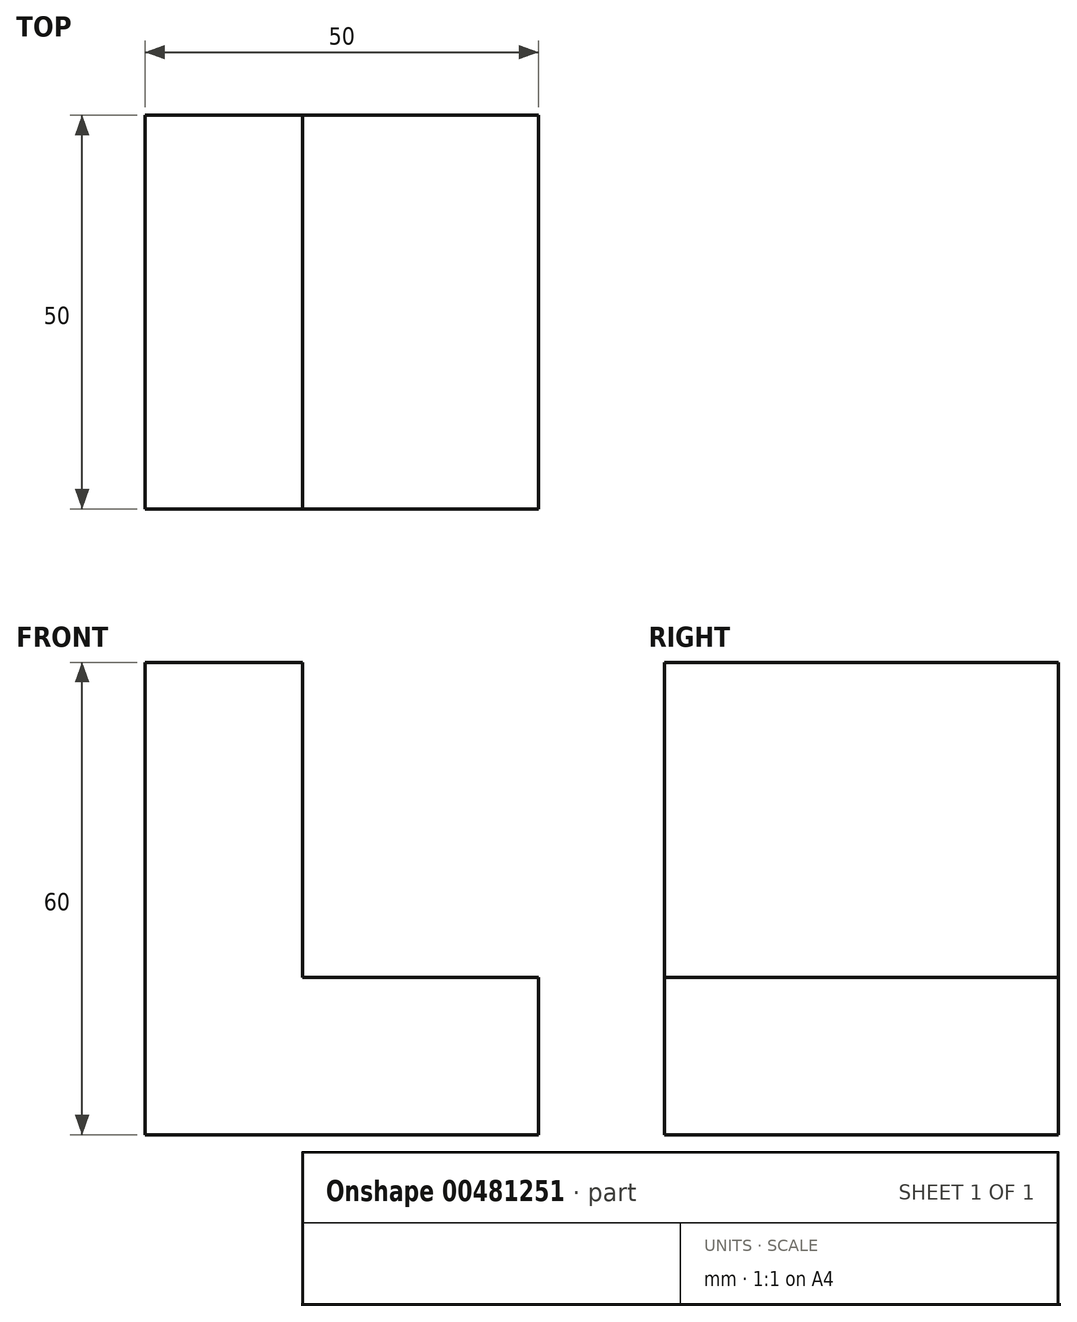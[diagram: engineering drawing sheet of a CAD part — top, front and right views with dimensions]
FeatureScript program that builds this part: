
annotation { "Feature Type Name" : "Feature", "Feature Type Description" : "" }
export const myFeature = defineFeature(function(context is Context, id is Id, definition is map)
    precondition{}
    {
        {
            var Q0;
            Q0=qCreatedBy(makeId("Front.planeOp"),FACE);
            var sketch = newSketch(context, id + "F0", { "sketchPlane" : qUnion([Q0])});
            skLineSegment(sketch, "E0", {"start": v(0, 0) * mm, "end": v(50, 0) * mm});
            skLineSegment(sketch, "E1", {"start": v(50, 0) * mm, "end": v(50, 20) * mm});
            skLineSegment(sketch, "E2", {"start": v(50, 20) * mm, "end": v(20, 20) * mm});
            skLineSegment(sketch, "E3", {"start": v(20, 20) * mm, "end": v(20, 60) * mm});
            skLineSegment(sketch, "E4", {"start": v(20, 60) * mm, "end": v(0, 60) * mm});
            skLineSegment(sketch, "E5", {"start": v(0, 60) * mm, "end": v(0, 0) * mm});
            skSolve(sketch);
        }
        {
            var Q0;
            Q0 = qSketchRegion(id + "F0", true);
            extrude(context, id + "F1", {"entities" : qUnion([Q0]), "depth" : 50 * mm});
        }
    });
